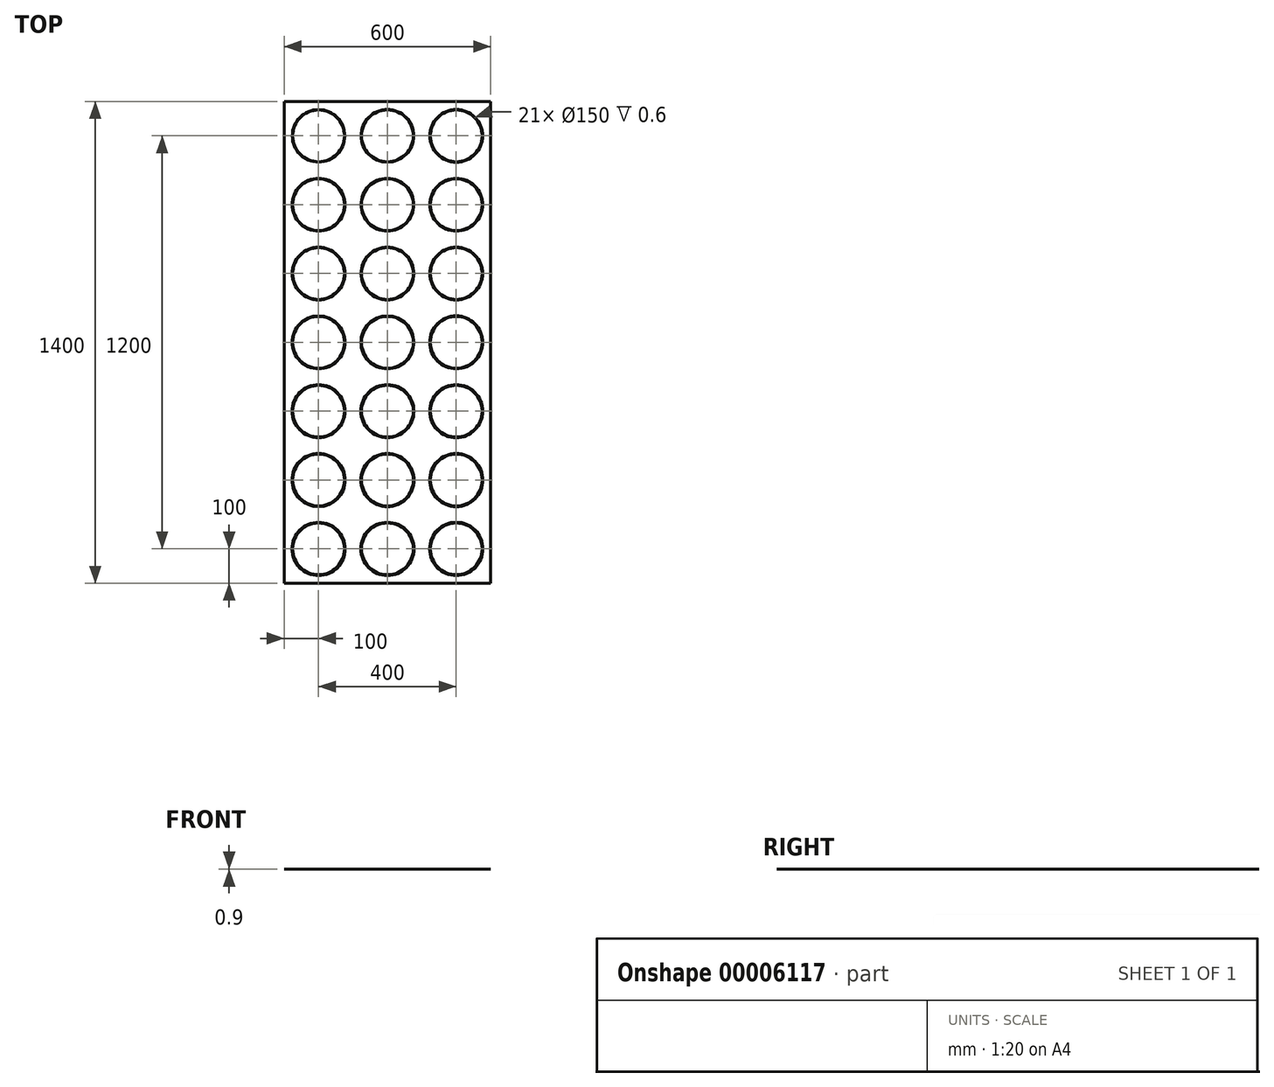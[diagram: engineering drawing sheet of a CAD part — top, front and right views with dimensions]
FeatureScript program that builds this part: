
annotation { "Feature Type Name" : "Feature", "Feature Type Description" : "" }
export const myFeature = defineFeature(function(context is Context, id is Id, definition is map)
    precondition{}
    {
        {
            var Q0;
            Q0=qCreatedBy(makeId("Top.planeOp"),FACE);
            var sketch = newSketch(context, id + "F0", { "sketchPlane" : qUnion([Q0])});
            skLineSegment(sketch, "E0.bottom", {"start": v(-100, 100) * mm, "end": v(500, 100) * mm});
            skLineSegment(sketch, "E0.top", {"start": v(-100, -1300) * mm, "end": v(500, -1300) * mm});
            skLineSegment(sketch, "E0.left", {"start": v(-100, 100) * mm, "end": v(-100, -1300) * mm});
            skLineSegment(sketch, "E0.right", {"start": v(500, 100) * mm, "end": v(500, -1300) * mm});
            skSolve(sketch);
        }
        {
            var Q0;
            Q0 = qSketchRegion(id + "F0", true);
            extrude(context, id + "F1", {"entities" : qUnion([Q0]), "depth" : 0.3 * mm});
        }
        {
            var Q0;
            Q0=makeQuery(id+"F1.opExtrude","CAP_FACE",FACE,{"disambiguationData":[OSD([sQuery(id+"F0.wireOp",EDGE,"E0.bottom"),sQuery(id+"F0.wireOp",EDGE,"E0.top"),sQuery(id+"F0.wireOp",EDGE,"E0.left"),sQuery(id+"F0.wireOp",EDGE,"E0.right")])],"isStart":false});
            var sketch = newSketch(context, id + "F2", { "sketchPlane" : qUnion([Q0])});
            skCircle(sketch, "E1", {"center": v(0, 0) * mm, "radius": 75 * mm});
            skCircle(sketch, "E2", {"center": v(0, 0) * mm, "radius": 76.5 * mm});
            skCircle(sketch, "E3", {"center": v(200, 0) * mm, "radius": 75 * mm});
            skCircle(sketch, "E4", {"center": v(200, 0) * mm, "radius": 76.6 * mm});
            skCircle(sketch, "E5", {"center": v(400, 0) * mm, "radius": 75 * mm});
            skCircle(sketch, "E6", {"center": v(400, 0) * mm, "radius": 76.7 * mm});
            skCircle(sketch, "E7", {"center": v(0, -200) * mm, "radius": 75 * mm});
            skCircle(sketch, "E8", {"center": v(0, -200) * mm, "radius": 76.75 * mm});
            skCircle(sketch, "E9", {"center": v(200, -200) * mm, "radius": 75 * mm});
            skCircle(sketch, "E10", {"center": v(200, -200) * mm, "radius": 76.8 * mm});
            skCircle(sketch, "E11", {"center": v(400, -200) * mm, "radius": 75 * mm});
            skCircle(sketch, "E12", {"center": v(400, -200) * mm, "radius": 76.85 * mm});
            skCircle(sketch, "E13", {"center": v(0, -400) * mm, "radius": 75 * mm});
            skCircle(sketch, "E14", {"center": v(0, -400) * mm, "radius": 76.9 * mm});
            skCircle(sketch, "E15", {"center": v(200, -400) * mm, "radius": 76.95 * mm});
            skCircle(sketch, "E16", {"center": v(200, -400) * mm, "radius": 75 * mm});
            skCircle(sketch, "E17", {"center": v(400, -400) * mm, "radius": 77 * mm});
            skCircle(sketch, "E18", {"center": v(400, -400) * mm, "radius": 75 * mm});
            skCircle(sketch, "E19", {"center": v(400, -800) * mm, "radius": 75 * mm});
            skCircle(sketch, "E20", {"center": v(400, -600) * mm, "radius": 75 * mm});
            skCircle(sketch, "E21", {"center": v(200, -600) * mm, "radius": 77.1 * mm});
            skCircle(sketch, "E22", {"center": v(200, -600) * mm, "radius": 75 * mm});
            skCircle(sketch, "E23", {"center": v(400, -800) * mm, "radius": 77.3 * mm});
            skCircle(sketch, "E24", {"center": v(0, -800) * mm, "radius": 75 * mm});
            skCircle(sketch, "E25", {"center": v(400, -600) * mm, "radius": 77.15 * mm});
            skCircle(sketch, "E26", {"center": v(0, -600) * mm, "radius": 77.05 * mm});
            skCircle(sketch, "E27", {"center": v(200, -800) * mm, "radius": 75 * mm});
            skCircle(sketch, "E28", {"center": v(0, -600) * mm, "radius": 75 * mm});
            skCircle(sketch, "E29", {"center": v(200, -800) * mm, "radius": 77.25 * mm});
            skCircle(sketch, "E30", {"center": v(0, -800) * mm, "radius": 77.2 * mm});
            skCircle(sketch, "E31", {"center": v(0, -1200) * mm, "radius": 77.5 * mm});
            skCircle(sketch, "E32", {"center": v(200, -1200) * mm, "radius": 77.55 * mm});
            skCircle(sketch, "E33", {"center": v(0, -1000) * mm, "radius": 77.35 * mm});
            skCircle(sketch, "E34", {"center": v(400, -1000) * mm, "radius": 77.45 * mm});
            skCircle(sketch, "E35", {"center": v(200, -1000) * mm, "radius": 77.4 * mm});
            skCircle(sketch, "E36", {"center": v(0, -1200) * mm, "radius": 75 * mm});
            skCircle(sketch, "E37", {"center": v(400, -1200) * mm, "radius": 75 * mm});
            skCircle(sketch, "E38", {"center": v(400, -1200) * mm, "radius": 77.6 * mm});
            skCircle(sketch, "E39", {"center": v(200, -1000) * mm, "radius": 75 * mm});
            skCircle(sketch, "E40", {"center": v(0, -1000) * mm, "radius": 75 * mm});
            skCircle(sketch, "E41", {"center": v(400, -1000) * mm, "radius": 75 * mm});
            skCircle(sketch, "E42", {"center": v(200, -1200) * mm, "radius": 75 * mm});
            skSolve(sketch);
        }
        {
            var Q0;
            Q0 = qSketchRegion(id + "F2", true);
            extrude(context, id + "F3", {"entities" : qUnion([Q0]), "operationType" : NewBodyOperationType.ADD, "depth" : 0.6 * mm});
        }
    });
